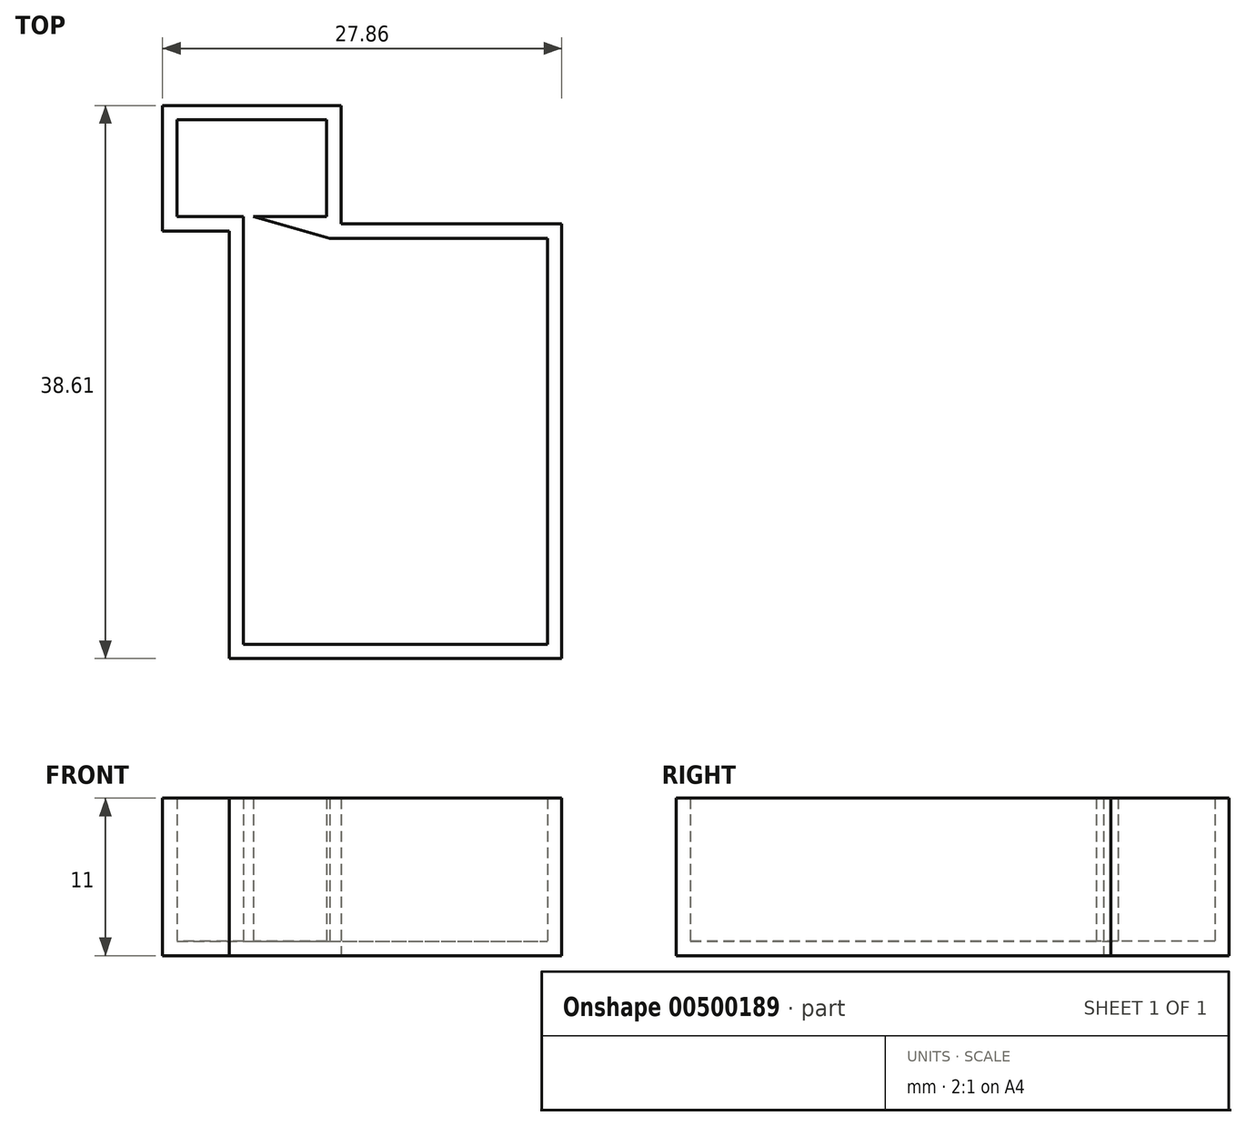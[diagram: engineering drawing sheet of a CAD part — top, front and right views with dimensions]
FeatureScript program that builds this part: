
annotation { "Feature Type Name" : "Feature", "Feature Type Description" : "" }
export const myFeature = defineFeature(function(context is Context, id is Id, definition is map)
    precondition{}
    {
        {
            var Q0;
            Q0=qCreatedBy(makeId("Top.planeOp"),FACE);
            var sketch = newSketch(context, id + "F0", { "sketchPlane" : qUnion([Q0])});
            skLineSegment(sketch, "E0.bottom", {"start": v(-48.9, 46.66) * mm, "end": v(-33.7, 46.66) * mm});
            skLineSegment(sketch, "E0.top", {"start": v(-54.92, 18.3) * mm, "end": v(-33.7, 18.3) * mm});
            skLineSegment(sketch, "E0.left", {"start": v(-54.92, 46.66) * mm, "end": v(-54.92, 18.3) * mm});
            skLineSegment(sketch, "E0.right", {"start": v(-33.7, 46.66) * mm, "end": v(-33.7, 18.3) * mm});
            skLineSegment(sketch, "E1", {"start": v(-54.92, 46.66) * mm, "end": v(-54.92, 48.16) * mm});
            skLineSegment(sketch, "E2", {"start": v(-54.92, 48.16) * mm, "end": v(-59.57, 48.16) * mm});
            skLineSegment(sketch, "E3", {"start": v(-59.57, 48.16) * mm, "end": v(-59.57, 54.92) * mm});
            skLineSegment(sketch, "E4", {"start": v(-59.57, 54.92) * mm, "end": v(-49.1, 54.92) * mm});
            skLineSegment(sketch, "E5", {"start": v(-49.1, 54.92) * mm, "end": v(-49.1, 48.16) * mm});
            skLineSegment(sketch, "E6", {"start": v(-49.1, 48.16) * mm, "end": v(-54.25, 48.16) * mm});
            skLineSegment(sketch, "E7", {"start": v(-54.25, 48.16) * mm, "end": v(-48.9, 46.66) * mm});
            skSolve(sketch);
        }
        {
            var Q0;
            Q0 = qSketchRegion(id + "F0", true);
            extrude(context, id + "F1", {"entities" : qUnion([Q0]), "depth" : 10 * mm});
        }
        {
            var Q0;
            Q0=makeQuery(id+"F1.opExtrude","CAP_FACE",FACE,{"disambiguationData":[OSD([sQuery(id+"F0.wireOp",EDGE,"E0.bottom"),sQuery(id+"F0.wireOp",EDGE,"E0.top"),sQuery(id+"F0.wireOp",EDGE,"E0.left"),sQuery(id+"F0.wireOp",EDGE,"E0.right"),sQuery(id+"F0.wireOp",EDGE,"E1"),sQuery(id+"F0.wireOp",EDGE,"E2"),sQuery(id+"F0.wireOp",EDGE,"E3"),sQuery(id+"F0.wireOp",EDGE,"E4"),sQuery(id+"F0.wireOp",EDGE,"E5"),sQuery(id+"F0.wireOp",EDGE,"E6"),sQuery(id+"F0.wireOp",EDGE,"E7")])],"isStart":false});
            shell(context, id + "F2", {"entities" : qUnion([Q0]), "thickness" : 1 * mm, "oppositeDirection" : true});
        }
    });
